FCSTD DOCUMENT  (FreeCAD 0.18R13999 +4 (Git))
Label: test-S2R
License: All rights reserved
LicenseURL: http://en.wikipedia.org/wiki/All_rights_reserved
objects: Part::Feature×5, Part::Compound×2
note: 7 computed .brp shape members not serialized (recipe doc carries the construction recipe); baked Part::Feature solids carry a one-line shape summary decoded from their .brp

FEATURE [Part::Feature] Spline003_Edge1
  shape: bbox 0.9162 x 0.1611 x 1.413 mm, 0 faces, 0 solids (baked)
FEATURE [Part::Feature] Spline002_Edge1
  shape: bbox 1.009 x 0.7925 x 1.695 mm, 0 faces, 0 solids (baked)
FEATURE [Part::Feature] Spline004_Edge1
  shape: bbox 0.3832 x 1 x 0.8874 mm, 0 faces, 0 solids (baked)
FEATURE [Part::Feature] Spline005_Edge1
  shape: bbox 0.5195 x 1.688 x 0.6851 mm, 0 faces, 0 solids (baked)
FEATURE [Part::Feature] Shape001_Edge3_Edge1
  shape: bbox 2e-07 x 1 x 0.5284 mm, 0 faces, 0 solids (baked)
FEATURE [Part::Compound] Compound
  Links = -> [Spline002_Edge1,Spline003_Edge1]
FEATURE [Part::Compound] Compound001
  Links = -> [Spline004_Edge1,Shape001_Edge3_Edge1]
